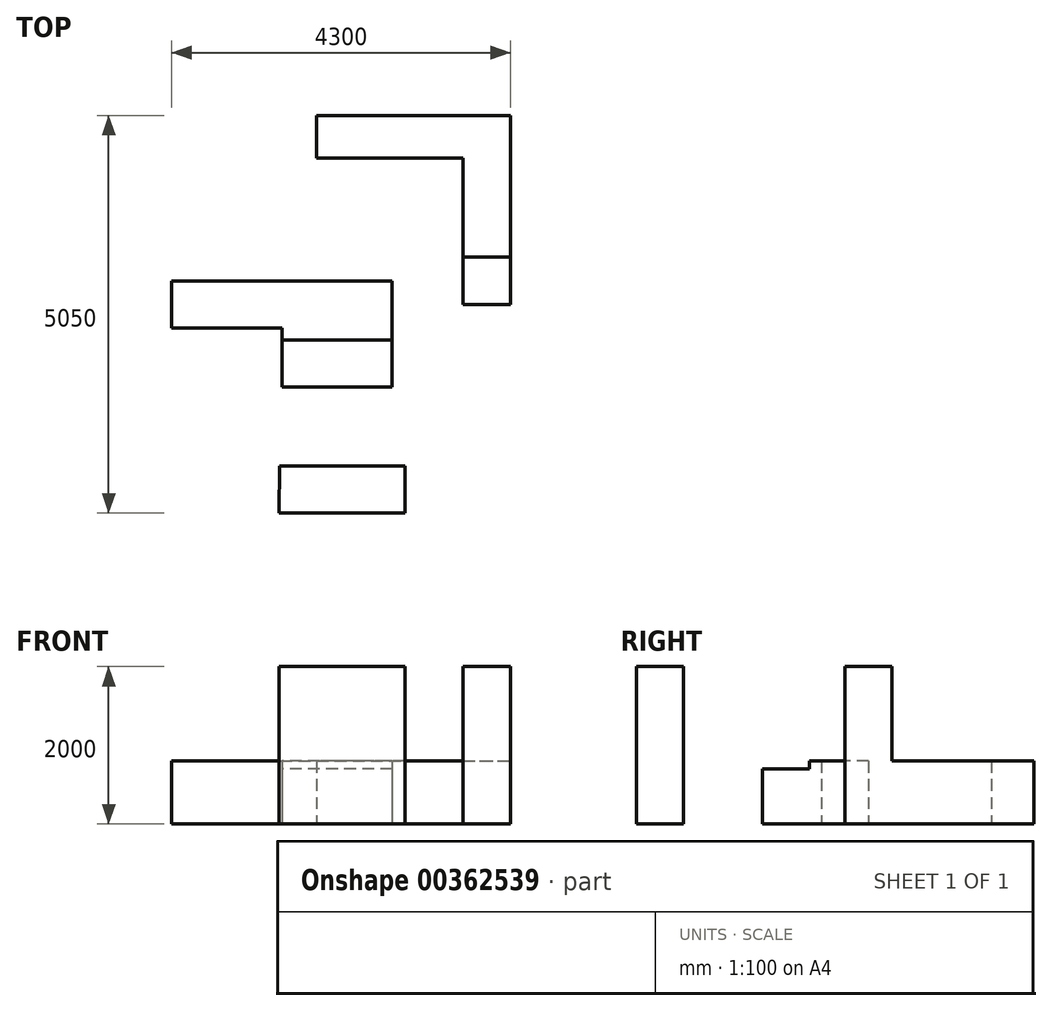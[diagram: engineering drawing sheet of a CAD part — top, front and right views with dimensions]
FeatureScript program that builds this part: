
annotation { "Feature Type Name" : "Feature", "Feature Type Description" : "" }
export const myFeature = defineFeature(function(context is Context, id is Id, definition is map)
    precondition{}
    {
        {
            var Q0;
            Q0=qCreatedBy(makeId("Top.planeOp"),FACE);
            var sketch = newSketch(context, id + "F0", { "sketchPlane" : qUnion([Q0])});
            skLineSegment(sketch, "E0", {"start": v(-1399.4, 0) * mm, "end": v(0, 0) * mm});
            skLineSegment(sketch, "E1", {"start": v(0, 0) * mm, "end": v(-39.4, -2350) * mm});
            skLineSegment(sketch, "E2", {"start": v(2950.6, -490) * mm, "end": v(2770.6, -490) * mm});
            skLineSegment(sketch, "E3", {"start": v(2770.6, -490) * mm, "end": v(2770.6, -70) * mm});
            skLineSegment(sketch, "E4", {"start": v(2900.6, 300) * mm, "end": v(2900.6, 2700) * mm});
            skPoint(sketch, "E5", {"position": v(-1399.4, 2700) * mm});
            skPoint(sketch, "E6", {"position": v(-579.4, 2700) * mm});
            skPoint(sketch, "E7", {"position": v(490.6, 2700) * mm});
            skPoint(sketch, "E8", {"position": v(2150.6, 2700) * mm});
            skPoint(sketch, "E9", {"position": v(-1399.4, 1890) * mm});
            skPoint(sketch, "E10", {"position": v(-1399.4, 1680) * mm});
            skPoint(sketch, "E11", {"position": v(-1399.4, 720) * mm});
            skLineSegment(sketch, "E12", {"start": v(2900.6, 300) * mm, "end": v(2300.6, 300) * mm});
            skLineSegment(sketch, "E13", {"start": v(2300.6, -70) * mm, "end": v(2300.6, 300) * mm});
            skLineSegment(sketch, "E14", {"start": v(2300.6, -70) * mm, "end": v(2770.6, -70) * mm});
            skLineSegment(sketch, "E15", {"start": v(2950.6, -490) * mm, "end": v(2950.6, -750) * mm});
            skLineSegment(sketch, "E16", {"start": v(-579.4, 2700) * mm, "end": v(490.6, 2700) * mm});
            skLineSegment(sketch, "E17", {"start": v(2150.6, 2700) * mm, "end": v(2900.6, 2700) * mm});
            skLineSegment(sketch, "E18", {"start": v(-1399.4, 1890) * mm, "end": v(-1399.4, 1680) * mm});
            skLineSegment(sketch, "E19", {"start": v(-1399.4, 720) * mm, "end": v(-1399.4, 0) * mm});
            skLineSegment(sketch, "E20", {"start": v(2950.6, -1560) * mm, "end": v(2950.6, -2350) * mm});
            skLineSegment(sketch, "E21", {"start": v(2950.6, -2350) * mm, "end": v(2620.6, -2350) * mm});
            skPoint(sketch, "E22", {"position": v(1660.6, -2350) * mm});
            skLineSegment(sketch, "E23", {"start": v(1660.6, -2350) * mm, "end": v(-39.4, -2350) * mm});
            skLineSegment(sketch, "E24", {"start": v(490.6, 2700) * mm, "end": v(2150.6, 2700) * mm});
            skLineSegment(sketch, "E25", {"start": v(-1399.4, 2700) * mm, "end": v(-579.4, 2700) * mm});
            skLineSegment(sketch, "E26", {"start": v(-1399.4, 2700) * mm, "end": v(-1399.4, 1890) * mm});
            skLineSegment(sketch, "E27", {"start": v(-1399.4, 1680) * mm, "end": v(-1399.4, 720) * mm});
            skLineSegment(sketch, "E28", {"start": v(2950.6, -750) * mm, "end": v(2950.6, -1560) * mm});
            skLineSegment(sketch, "E29", {"start": v(2620.6, -2350) * mm, "end": v(1660.6, -2350) * mm});
            skLineSegment(sketch, "E30", {"start": v(-1399.4, 600) * mm, "end": v(1400.6, 600) * mm});
            skLineSegment(sketch, "E31", {"start": v(1400.6, 600) * mm, "end": v(1400.6, -750) * mm});
            skLineSegment(sketch, "E32", {"start": v(1400.6, -750) * mm, "end": v(0, -750) * mm});
            skLineSegment(sketch, "E33.bottom", {"start": v(-39.4, -2350) * mm, "end": v(1560.6, -2350) * mm, "construction": true});
            skLineSegment(sketch, "E33.top", {"start": v(-39.4, -1750) * mm, "end": v(1560.6, -1750) * mm});
            skLineSegment(sketch, "E33.left", {"start": v(-39.4, -2350) * mm, "end": v(-39.4, -1750) * mm});
            skLineSegment(sketch, "E33.right", {"start": v(1560.6, -2350) * mm, "end": v(1560.6, -1750) * mm});
            skLineSegment(sketch, "E34", {"start": v(0, -750) * mm, "end": v(0, 0) * mm});
            skLineSegment(sketch, "E35", {"start": v(2300.6, 2162.58) * mm, "end": v(2300.6, 300) * mm});
            skLineSegment(sketch, "E36", {"start": v(2300.6, 2162.58) * mm, "end": v(440.34, 2162.58) * mm});
            skLineSegment(sketch, "E37", {"start": v(440.34, 2162.58) * mm, "end": v(440.34, 2700) * mm});
            skLineSegment(sketch, "E38", {"start": v(440.34, 2700) * mm, "end": v(2900.6, 2700) * mm});
            skLineSegment(sketch, "E39", {"start": v(2300.6, 900) * mm, "end": v(2900.6, 900) * mm});
            skLineSegment(sketch, "E40", {"start": v(1400.6, -150) * mm, "end": v(-2.52, -150) * mm});
            skSolve(sketch);
        }
        {
            var Q0;
            Q0=makeQuery(id+"F0.imprint","IMPRINT",FACE,{"disambiguationData":[TD([[makeQuery(id+"F0.imprint","IMPRINT",EDGE,{"derivedFrom":sQuery(id+"F0.wireOp",EDGE,"E0")}),1.0]])]});
            var Q1;
            Q1=sQuery(id+"F0.wireOp",EDGE,"E17");
            var Q2;
            Q2=sQuery(id+"F0.wireOp",EDGE,"E4");
            var Q3;
            Q3=sQuery(id+"F0.wireOp",EDGE,"E12");
            var Q4;
            Q4=sQuery(id+"F0.wireOp",EDGE,"E13");
            var Q5;
            Q5=sQuery(id+"F0.wireOp",EDGE,"E14");
            var Q6;
            Q6=sQuery(id+"F0.wireOp",EDGE,"E3");
            var Q7;
            Q7=sQuery(id+"F0.wireOp",EDGE,"E2");
            var Q8;
            Q8=sQuery(id+"F0.wireOp",EDGE,"E15");
            var Q9;
            Q9=sQuery(id+"F0.wireOp",EDGE,"E20");
            var Q10;
            Q10=sQuery(id+"F0.wireOp",EDGE,"E21");
            var Q11;
            Q11=sQuery(id+"F0.wireOp",EDGE,"E23");
            var Q12;
            Q12=sQuery(id+"F0.wireOp",EDGE,"E1");
            var Q13;
            Q13=sQuery(id+"F0.wireOp",EDGE,"E0");
            var Q14;
            Q14=sQuery(id+"F0.wireOp",EDGE,"E19");
            var Q15;
            Q15=sQuery(id+"F0.wireOp",EDGE,"E18");
            var Q16;
            Q16=sQuery(id+"F0.wireOp",EDGE,"E16");
            extrude(context, id + "F1", {"entities" : qUnion([Q0]), "bodyType" : ToolBodyType.SURFACE, "surfaceEntities" : qUnion([Q1, Q2, Q3, Q4, Q5, Q6, Q7, Q8, Q9, Q10, Q11, Q12, Q13, Q14, Q15, Q16]), "depth" : 2000 * mm});
        }
        {
            var Q0;
            Q0=sQuery(id+"F0.wireOp",EDGE,"E24");
            var Q1;
            Q1=sQuery(id+"F0.wireOp",EDGE,"E28");
            extrude(context, id + "F2", {"bodyType" : ToolBodyType.SURFACE, "surfaceEntities" : qUnion([Q0, Q1]), "depth" : 1000 * mm});
        }
        {
            var Q0;
            {var subQ1=sQuery(id+"F0.wireOp",EDGE,"E0");Q0=makeQuery(id+"F0.imprint","IMPRINT",FACE,{"disambiguationData":[TD([[makeQuery(id+"F0.imprint","IMPRINT",EDGE,{"derivedFrom":subQ1}),1.0]])]});}
            extrude(context, id + "F3", {"entities" : qUnion([Q0]), "depth" : 800 * mm});
        }
        {
            var Q0;
            {var subQ5=sQuery(id+"F0.wireOp",EDGE,"E33.right");Q0=makeQuery(id+"F0.imprint","IMPRINT",FACE,{"disambiguationData":[TD([[makeQuery(id+"F0.imprint","IMPRINT",EDGE,{"derivedFrom":subQ5}),1.0]])]});}
            extrude(context, id + "F4", {"entities" : qUnion([Q0]), "depth" : 2000 * mm});
        }
        {
            var Q0;
            Q0=makeQuery(id+"F0.imprint","IMPRINT",FACE,{"disambiguationData":[TD([[makeQuery(id+"F0.imprint","IMPRINT",EDGE,{"derivedFrom":sQuery(id+"F0.wireOp",EDGE,"E4")}),1.0]])]});
            var Q1;
            Q1=makeQuery(id+"F4.opExtrude","CAP_FACE",FACE,{"disambiguationData":[OSD([sQuery(id+"F0.wireOp",EDGE,"E1"),sQuery(id+"F0.wireOp",EDGE,"E23"),sQuery(id+"F0.wireOp",EDGE,"E33.top"),sQuery(id+"F0.wireOp",EDGE,"E33.right")])],"isStart":false});
            extrude(context, id + "F5", {"entities" : qUnion([Q0]), "endBound" : BoundingType.UP_TO_SURFACE, "endBoundEntityFace" : qUnion([Q1]), "depth" : 25 * mm});
        }
        {
            var Q0;
            {var subQ0=sQuery(id+"F0.wireOp",EDGE,"E36");Q0=makeQuery(id+"F0.imprint","IMPRINT",FACE,{"disambiguationData":[TD([[makeQuery(id+"F0.imprint","IMPRINT",EDGE,{"derivedFrom":subQ0}),-1.0]])]});}
            var Q1;
            Q1=makeQuery(id+"F3.opExtrude","CAP_FACE",FACE,{"disambiguationData":[OSD([sQuery(id+"F0.wireOp",EDGE,"E0"),sQuery(id+"F0.wireOp",EDGE,"E19"),sQuery(id+"F0.wireOp",EDGE,"E30"),sQuery(id+"F0.wireOp",EDGE,"E31"),sQuery(id+"F0.wireOp",EDGE,"E32"),sQuery(id+"F0.wireOp",EDGE,"E34")])],"isStart":false});
            extrude(context, id + "F6", {"entities" : qUnion([Q0]), "operationType" : NewBodyOperationType.ADD, "endBound" : BoundingType.UP_TO_SURFACE, "endBoundEntityFace" : qUnion([Q1]), "depth" : 25 * mm});
        }
        {
            var Q0;
            {var subQ0=sQuery(id+"F0.wireOp",EDGE,"E32");Q0=makeQuery(id+"F0.imprint","IMPRINT",FACE,{"disambiguationData":[TD([[makeQuery(id+"F0.imprint","IMPRINT",EDGE,{"derivedFrom":subQ0}),-1.0]])]});}
            extrude(context, id + "F7", {"entities" : qUnion([Q0]), "operationType" : NewBodyOperationType.ADD, "depth" : 700 * mm});
        }
    });
